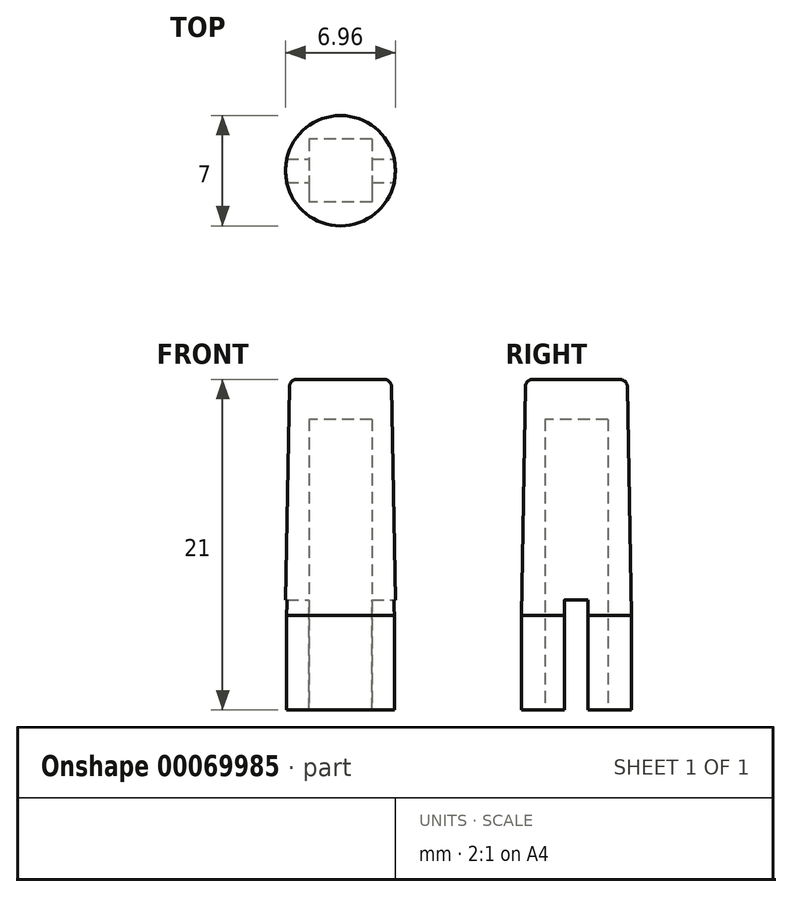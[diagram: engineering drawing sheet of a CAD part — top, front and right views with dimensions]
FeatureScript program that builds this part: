
annotation { "Feature Type Name" : "Feature", "Feature Type Description" : "" }
export const myFeature = defineFeature(function(context is Context, id is Id, definition is map)
    precondition{}
    {
        {
            var Q0;
            Q0=qCreatedBy(makeId("Top.planeOp"),FACE);
            var sketch = newSketch(context, id + "F0", { "sketchPlane" : qUnion([Q0])});
            skCircle(sketch, "E0", {"center": v(0, 0) * mm, "radius": 3.5 * mm});
            skSolve(sketch);
        }
        {
            var Q0;
            Q0=makeQuery(id+"F0.imprint","IMPRINT",FACE,{"disambiguationData":[TD([[makeQuery(id+"F0.imprint","IMPRINT",EDGE,{"derivedFrom":sQuery(id+"F0.wireOp",EDGE,"E0")}),1.0]])]});
            var Q1;
            Q1=sQuery(id+"F0.wireOp",EDGE,"E0");
            extrude(context, id + "F1", {"entities" : qUnion([Q0]), "surfaceEntities" : qUnion([Q1]), "depth" : 6 * mm});
        }
        {
            var Q0;
            Q0=makeQuery(id+"F1.opExtrude","CAP_FACE",FACE,{"disambiguationData":[OSD([sQuery(id+"F0.wireOp",EDGE,"E0")])],"isStart":false});
            extrude(context, id + "F2", {"entities" : qUnion([Q0]), "operationType" : NewBodyOperationType.ADD, "depth" : 15 * mm, "hasDraft" : true, "draftAngle" : 1 * degree, "draftPullDirection" : true});
        }
        {
            var Q0;
            Q0=makeQuery(id+"F1.opExtrude","CAP_FACE",FACE,{"disambiguationData":[OSD([sQuery(id+"F0.wireOp",EDGE,"E0")])],"isStart":true});
            var sketch = newSketch(context, id + "F3", { "sketchPlane" : qUnion([Q0])});
            skLineSegment(sketch, "E1.rect.bottom", {"start": v(2, -2) * mm, "end": v(-2, -2) * mm});
            skLineSegment(sketch, "E1.rect.top", {"start": v(2, 2) * mm, "end": v(-2, 2) * mm});
            skLineSegment(sketch, "E1.rect.left", {"start": v(2, -2) * mm, "end": v(2, 2) * mm});
            skLineSegment(sketch, "E1.rect.right", {"start": v(-2, -2) * mm, "end": v(-2, 2) * mm});
            skPoint(sketch, "E1.rect.middle", {"position": v(0, 0) * mm});
            skSolve(sketch);
        }
        {
            var Q0;
            Q0 = qSketchRegion(id + "F3", true);
            extrude(context, id + "F4", {"entities" : qUnion([Q0]), "operationType" : NewBodyOperationType.REMOVE, "oppositeDirection" : true, "depth" : 18.46 * mm});
        }
        {
            var Q0;
            Q0=qCreatedBy(makeId("Right.planeOp"),FACE);
            var sketch = newSketch(context, id + "F5", { "sketchPlane" : qUnion([Q0])});
            skLineSegment(sketch, "E2.rect.bottom", {"start": v(0.75, 0) * mm, "end": v(-0.75, 0) * mm});
            skLineSegment(sketch, "E2.rect.top", {"start": v(0.75, 7) * mm, "end": v(-0.75, 7) * mm});
            skLineSegment(sketch, "E2.rect.left", {"start": v(0.75, 0) * mm, "end": v(0.75, 7) * mm});
            skLineSegment(sketch, "E2.rect.right", {"start": v(-0.75, 0) * mm, "end": v(-0.75, 7) * mm});
            skPoint(sketch, "E2.rect.middle", {"position": v(0, 3.5) * mm});
            skSolve(sketch);
        }
        {
            var Q0;
            Q0 = qSketchRegion(id + "F5", true);
            extrude(context, id + "F6", {"entities" : qUnion([Q0]), "operationType" : NewBodyOperationType.REMOVE, "endBound" : BoundingType.THROUGH_ALL, "oppositeDirection" : true, "depth" : 25 * mm, "hasSecondDirection" : true, "secondDirectionBound" : BoundingType.THROUGH_ALL, "secondDirectionOppositeDirection" : false, "secondDirectionDepth" : 25 * mm});
        }
        {
            var Q0;
            Q0=makeQuery(id+"F2.opExtrude","CAP_EDGE",EDGE,{"disambiguationData":[OSD([sQuery(id+"F0.wireOp",EDGE,"E0")])],"isStart":false});
            fillet(context, id + "F7", {"entities" : qUnion([Q0]), "radius" : .5 * mm, "tangentPropagation" : true, "allowEdgeOverflow" : false});
        }
    });
